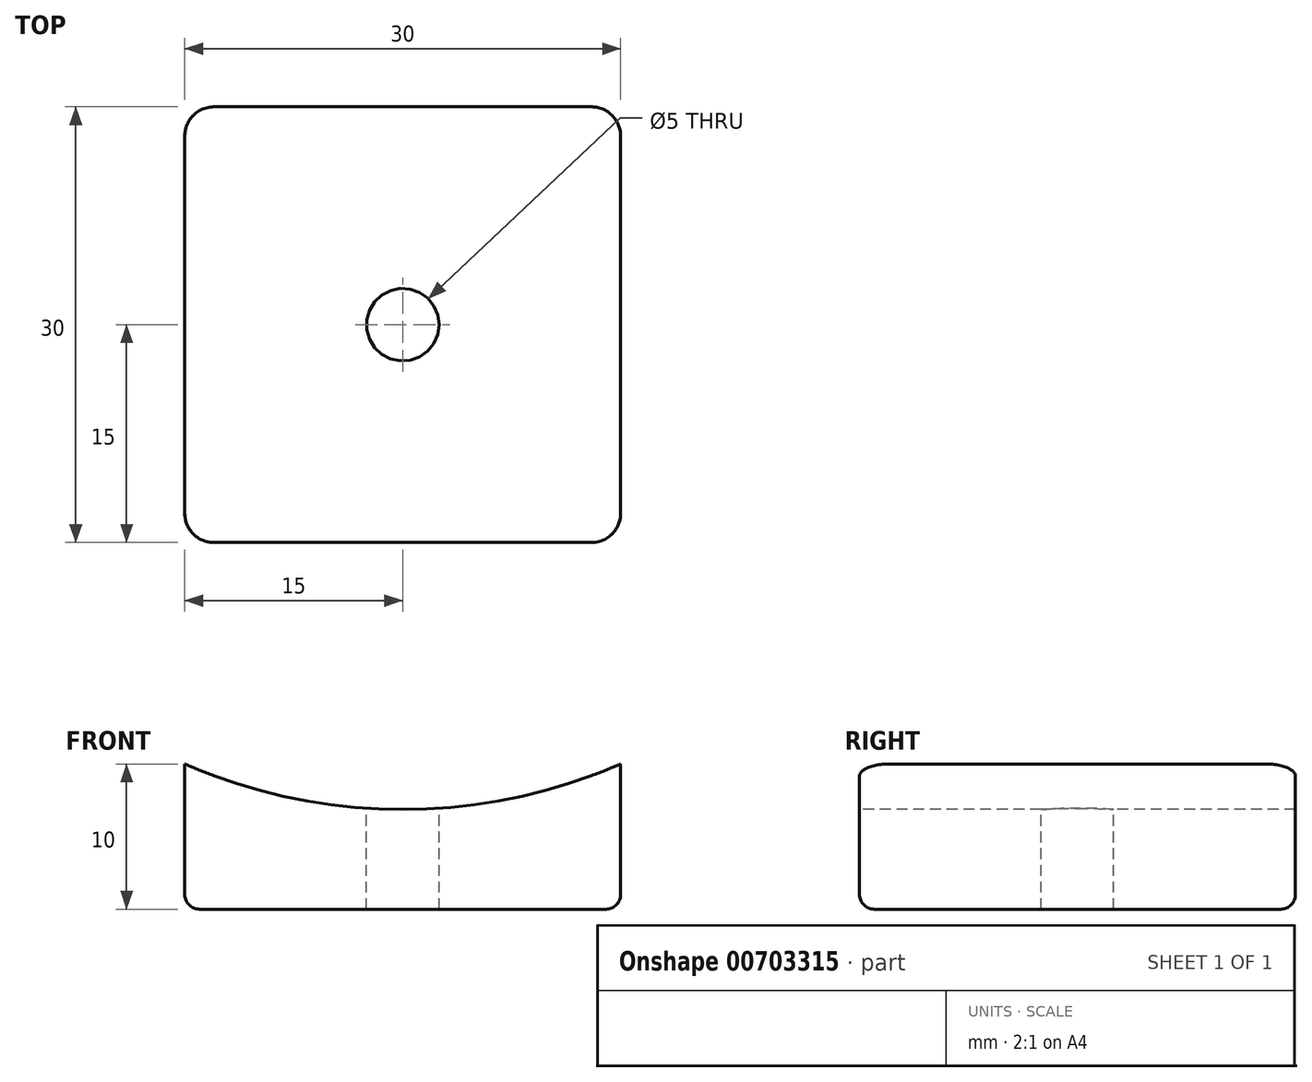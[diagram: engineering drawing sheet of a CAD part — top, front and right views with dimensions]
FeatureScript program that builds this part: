
annotation { "Feature Type Name" : "Feature", "Feature Type Description" : "" }
export const myFeature = defineFeature(function(context is Context, id is Id, definition is map)
    precondition{}
    {
        {
            var Q0;
            Q0=qCreatedBy(makeId("Top.planeOp"),FACE);
            var sketch = newSketch(context, id + "F0", { "sketchPlane" : qUnion([Q0])});
            skLineSegment(sketch, "E0.bottom", {"start": v(-15, -15) * mm, "end": v(15, -15) * mm});
            skLineSegment(sketch, "E0.top", {"start": v(-15, 15) * mm, "end": v(15, 15) * mm});
            skLineSegment(sketch, "E0.left", {"start": v(-15, -15) * mm, "end": v(-15, 15) * mm});
            skLineSegment(sketch, "E0.right", {"start": v(15, -15) * mm, "end": v(15, 15) * mm});
            skPoint(sketch, "E0.middle", {"position": v(0, 0) * mm});
            skSolve(sketch);
        }
        {
            var Q0;
            Q0=makeQuery(id+"F0.imprint","IMPRINT",FACE,{"disambiguationData":[TD([[makeQuery(id+"F0.imprint","IMPRINT",EDGE,{"derivedFrom":sQuery(id+"F0.wireOp",EDGE,"E0.bottom")}),1.0]])]});
            extrude(context, id + "F1", {"entities" : qUnion([Q0]), "depth" : 10 * mm, "offsetDistance" : 25 * mm});
        }
        {
            var Q0;
            Q0=makeQuery(id+"F1.opExtrude","SWEPT_FACE",FACE,{"disambiguationData":[OSD([sQuery(id+"F0.wireOp",EDGE,"E0.bottom")])]});
            var sketch = newSketch(context, id + "F2", { "sketchPlane" : qUnion([Q0])});
            skArc(sketch, "E1", {"start": v(-15, 10) * mm, "mid": v(0, 6.87) * mm, "end": v(15, 10) * mm});
            skSolve(sketch);
        }
        {
            var Q0;
            Q0=makeQuery(id+"F2.imprint","IMPRINT",FACE,{"disambiguationData":[TD([[makeQuery(id+"F2.imprint","IMPRINT",EDGE,{"derivedFrom":sQuery(id+"F2.wireOp",EDGE,"E1")}),1.0]])]});
            extrude(context, id + "F3", {"entities" : qUnion([Q0]), "operationType" : NewBodyOperationType.REMOVE, "oppositeDirection" : true, "depth" : 50 * mm, "offsetDistance" : 25 * mm});
        }
        {
            var Q0;
            Q0=makeQuery(id+"F1.opExtrude","CAP_FACE",FACE,{"disambiguationData":[OSD([sQuery(id+"F0.wireOp",EDGE,"E0.bottom"),sQuery(id+"F0.wireOp",EDGE,"E0.top"),sQuery(id+"F0.wireOp",EDGE,"E0.left"),sQuery(id+"F0.wireOp",EDGE,"E0.right")])],"isStart":true});
            var sketch = newSketch(context, id + "F4", { "sketchPlane" : qUnion([Q0])});
            skPoint(sketch, "E2", {"position": v(0, 0) * mm});
            skSolve(sketch);
        }
        {
            var Q0;
            Q0=sQuery(id+"F4.wireOp",VERTEX,"E2");
            var Q1;
            Q1=makeQuery(id+"F1.opExtrude","SWEPT_BODY",BODY,{"disambiguationData":[OSD([sQuery(id+"F0.wireOp",EDGE,"E0.bottom"),sQuery(id+"F0.wireOp",EDGE,"E0.top"),sQuery(id+"F0.wireOp",EDGE,"E0.left"),sQuery(id+"F0.wireOp",EDGE,"E0.right")])]});
            hole(context, id + "F5", {"style" : HoleStyle.SIMPLE, "endStyle" : HoleEndStyle.THROUGH, "holeDiameter" : 5 * mm, "majorDiameter" : 5 * mm, "isTappedThrough" : true, "tappedDepth" : 12 * mm, "tapClearance" : 3, "locations" : qUnion([Q0]), "scope" : qUnion([Q1])});
        }
        {
            var Q0;
            Q0=makeQuery(id+"F1.opExtrude","SWEPT_EDGE",EDGE,{"disambiguationData":[OSD([sQuery(id+"F0.wireOp",EDGE,"E0.bottom"),sQuery(id+"F0.wireOp",EDGE,"E0.left")])]});
            var Q1;
            Q1=makeQuery(id+"F1.opExtrude","SWEPT_EDGE",EDGE,{"disambiguationData":[OSD([sQuery(id+"F0.wireOp",EDGE,"E0.bottom"),sQuery(id+"F0.wireOp",EDGE,"E0.right")])]});
            var Q2;
            Q2=makeQuery(id+"F1.opExtrude","SWEPT_EDGE",EDGE,{"disambiguationData":[OSD([sQuery(id+"F0.wireOp",EDGE,"E0.top"),sQuery(id+"F0.wireOp",EDGE,"E0.right")])]});
            var Q3;
            Q3=makeQuery(id+"F1.opExtrude","SWEPT_EDGE",EDGE,{"disambiguationData":[OSD([sQuery(id+"F0.wireOp",EDGE,"E0.top"),sQuery(id+"F0.wireOp",EDGE,"E0.left")])]});
            fillet(context, id + "F6", {"entities" : qUnion([Q0, Q1, Q2, Q3]), "radius" : 2 * mm, "tangentPropagation" : true, "allowEdgeOverflow" : false});
        }
        {
            var Q0;
            Q0=makeQuery(id+"F1.opExtrude","CAP_EDGE",EDGE,{"disambiguationData":[OSD([sQuery(id+"F0.wireOp",EDGE,"E0.left")])],"isStart":true});
            fillet(context, id + "F7", {"entities" : qUnion([Q0]), "radius" : 1 * mm, "tangentPropagation" : true, "allowEdgeOverflow" : false});
        }
    });
